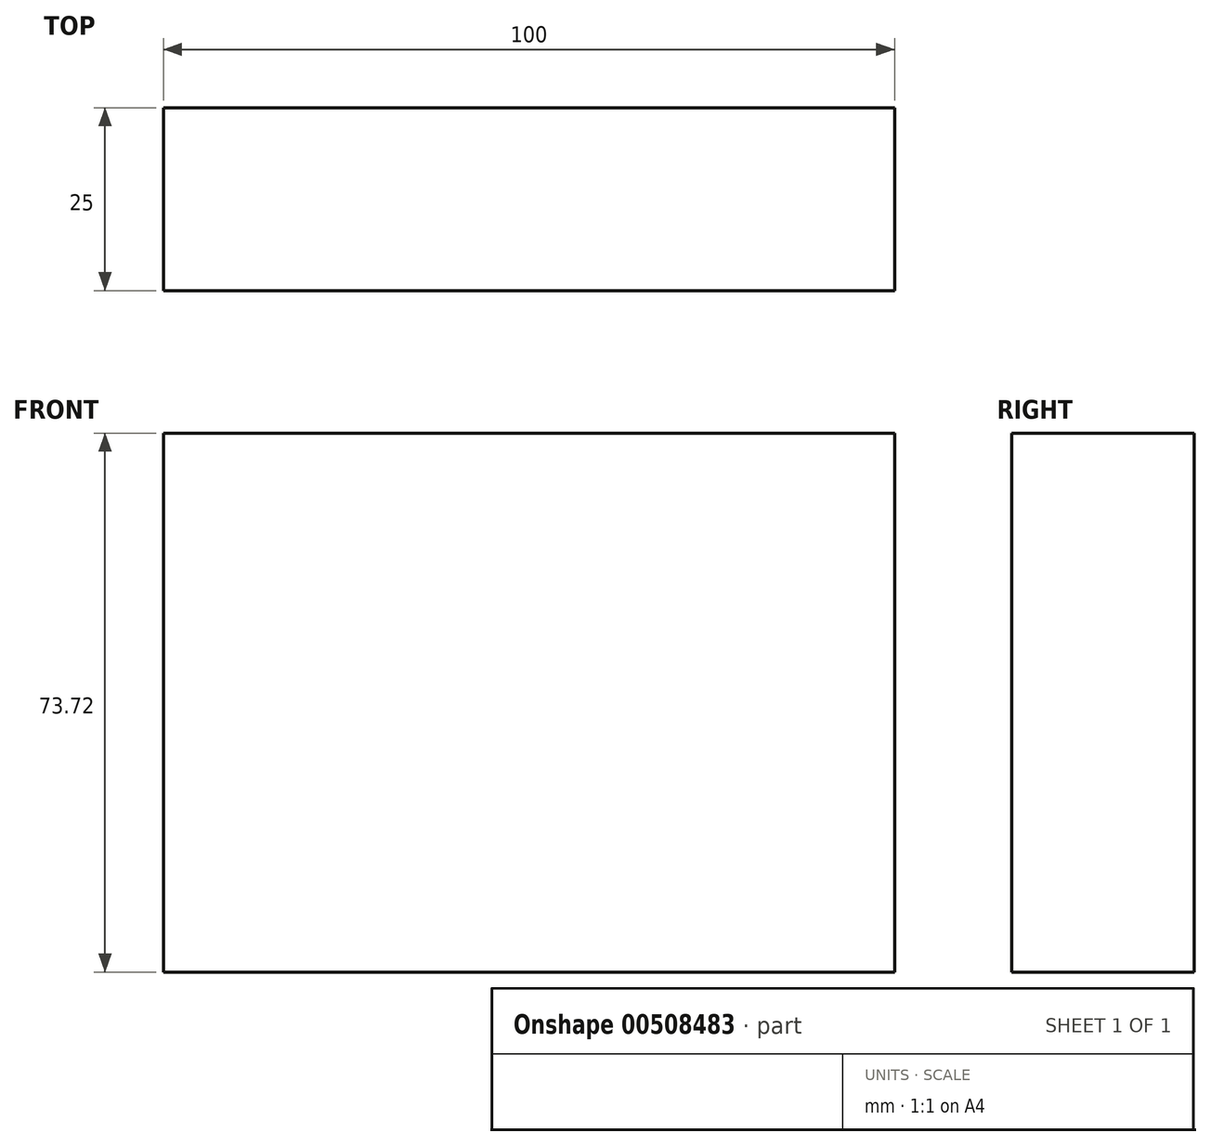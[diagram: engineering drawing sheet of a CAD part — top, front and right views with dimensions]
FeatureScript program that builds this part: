
annotation { "Feature Type Name" : "Feature", "Feature Type Description" : "" }
export const myFeature = defineFeature(function(context is Context, id is Id, definition is map)
    precondition{}
    {
        {
            var Q0;
            Q0=qCreatedBy(makeId("Front.planeOp"),FACE);
            var sketch = newSketch(context, id + "F0", { "sketchPlane" : qUnion([Q0])});
            skLineSegment(sketch, "E0.bottom", {"start": v(-50.84, 39.61) * mm, "end": v(49.16, 39.61) * mm});
            skLineSegment(sketch, "E0.top", {"start": v(-50.84, -34.11) * mm, "end": v(49.16, -34.11) * mm});
            skLineSegment(sketch, "E0.left", {"start": v(-50.84, 39.61) * mm, "end": v(-50.84, -34.11) * mm});
            skLineSegment(sketch, "E0.right", {"start": v(49.16, 39.61) * mm, "end": v(49.16, -34.11) * mm});
            skSolve(sketch);
        }
        {
            var Q0;
            Q0=makeQuery(id+"F0.imprint","IMPRINT",FACE,{"disambiguationData":[TD([[makeQuery(id+"F0.imprint","IMPRINT",EDGE,{"derivedFrom":sQuery(id+"F0.wireOp",EDGE,"E0.bottom")}),-1.0]])]});
            extrude(context, id + "F1", {"entities" : qUnion([Q0]), "depth" : 25 * mm});
        }
    });
